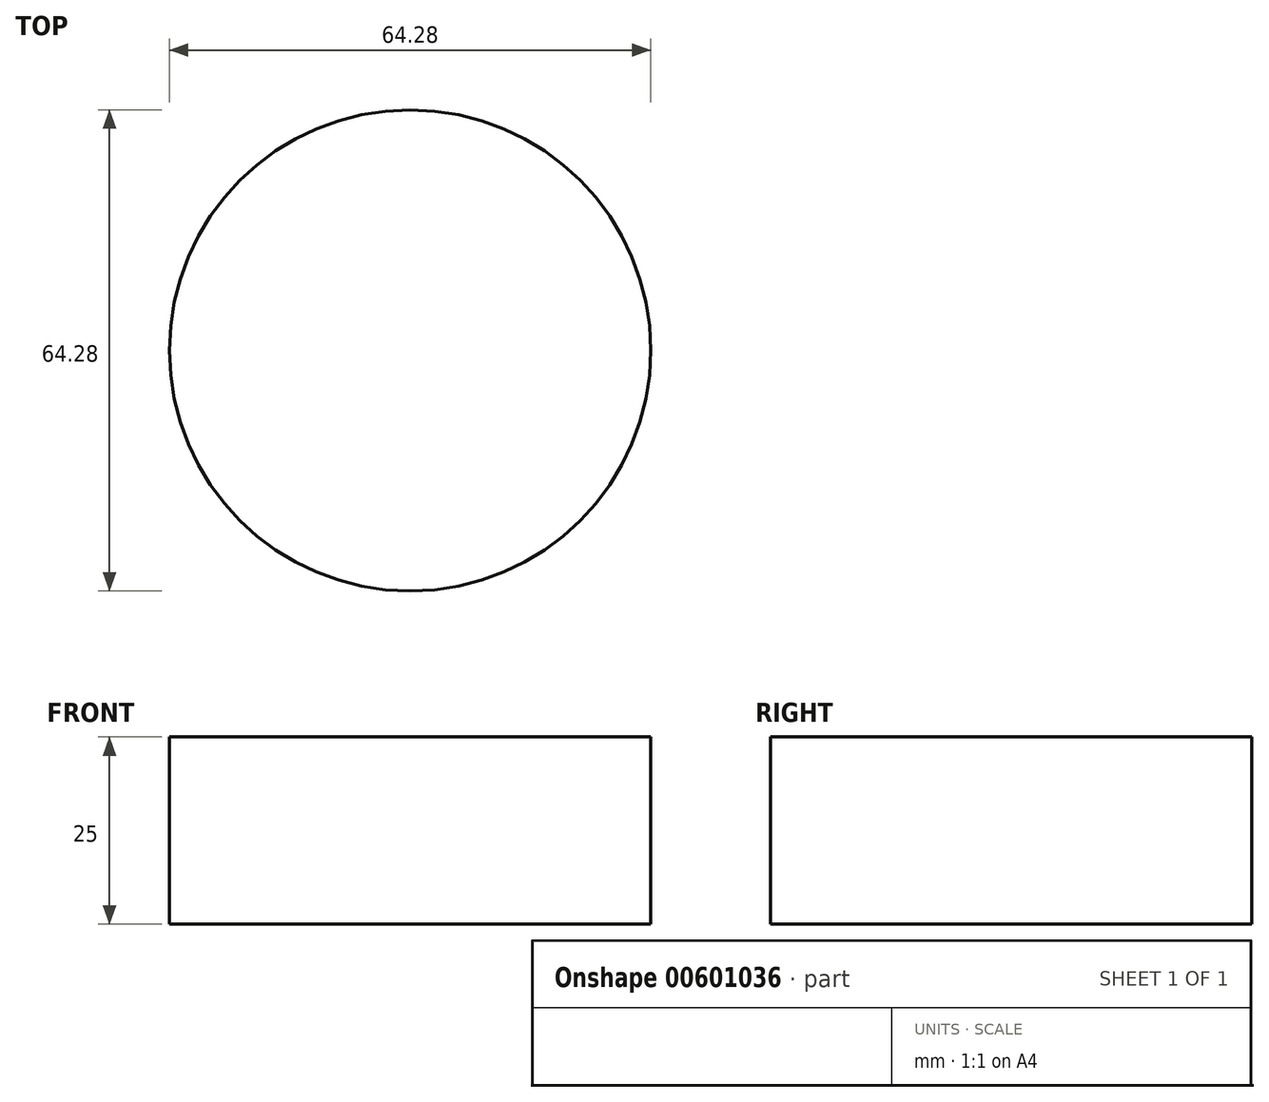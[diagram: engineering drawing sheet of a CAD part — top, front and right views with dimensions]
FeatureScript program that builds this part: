
annotation { "Feature Type Name" : "Feature", "Feature Type Description" : "" }
export const myFeature = defineFeature(function(context is Context, id is Id, definition is map)
    precondition{}
    {
        {
            var Q0;
            Q0=qCreatedBy(makeId("Top.planeOp"),FACE);
            var sketch = newSketch(context, id + "F0", { "sketchPlane" : qUnion([Q0])});
            skCircle(sketch, "E0", {"center": v(0, 0) * mm, "radius": 32.14 * mm});
            skSolve(sketch);
        }
        {
            var Q0;
            Q0 = qSketchRegion(id + "F0", true);
            extrude(context, id + "F1", {"entities" : qUnion([Q0]), "depth" : 25 * mm, "offsetDistance" : 25 * mm});
        }
    });
